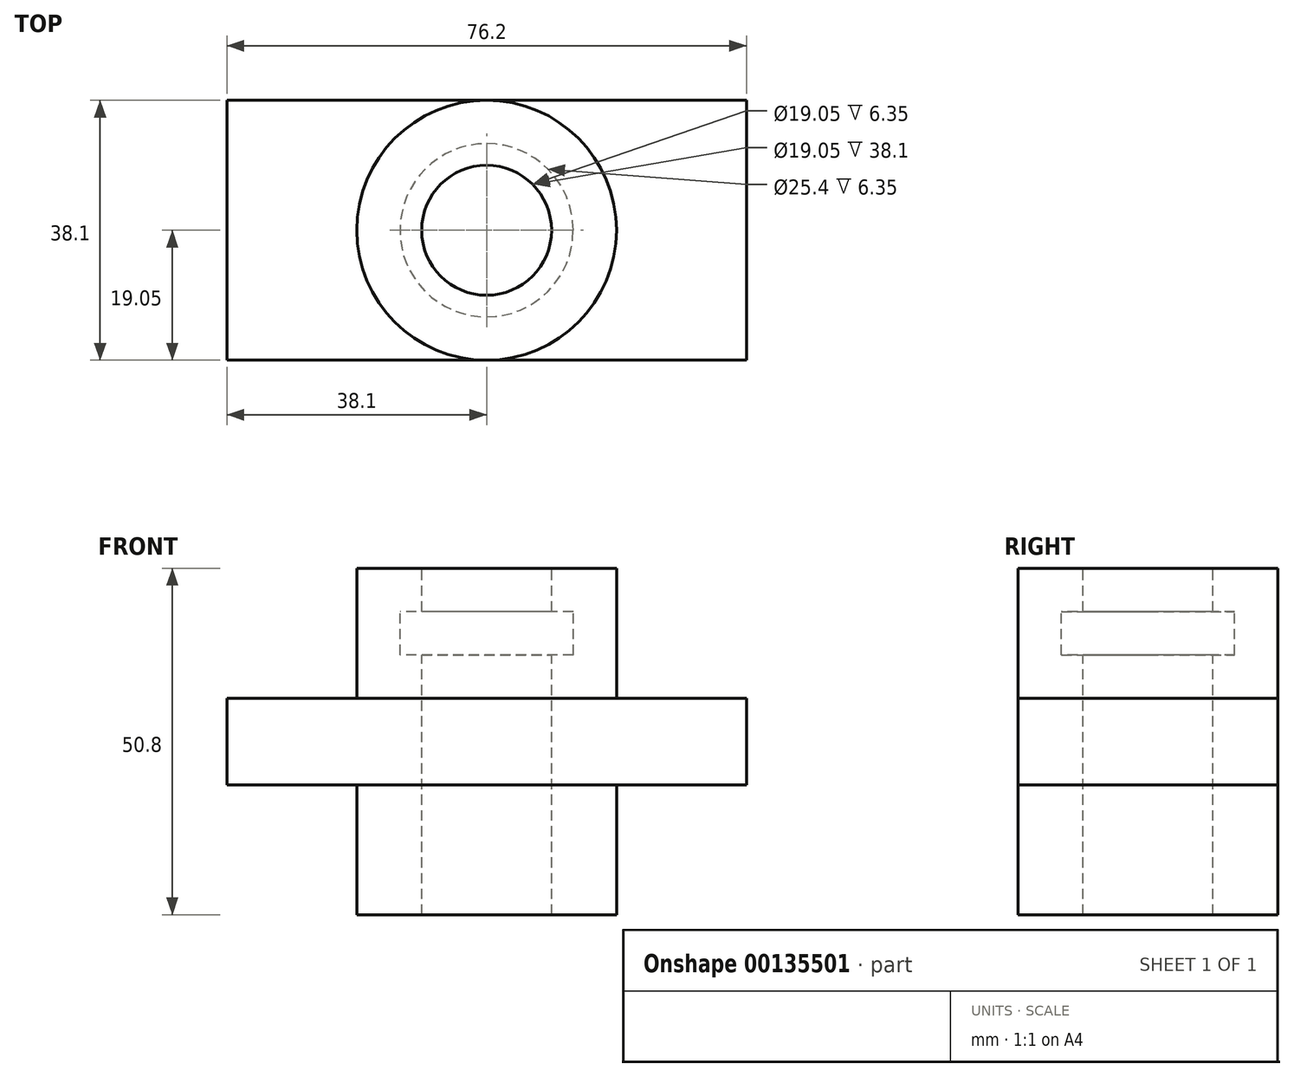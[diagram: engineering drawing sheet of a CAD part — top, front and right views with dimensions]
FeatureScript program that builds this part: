
annotation { "Feature Type Name" : "Feature", "Feature Type Description" : "" }
export const myFeature = defineFeature(function(context is Context, id is Id, definition is map)
    precondition{}
    {
        {
            var Q0;
            Q0=qCreatedBy(makeId("Top.planeOp"),FACE);
            var sketch = newSketch(context, id + "F0", { "sketchPlane" : qUnion([Q0])});
            skLineSegment(sketch, "E0.bottom", {"start": v(38.1, 19.05) * mm, "end": v(-38.1, 19.05) * mm});
            skLineSegment(sketch, "E0.top", {"start": v(38.1, -19.05) * mm, "end": v(-38.1, -19.05) * mm});
            skLineSegment(sketch, "E0.left", {"start": v(38.1, 19.05) * mm, "end": v(38.1, -19.05) * mm});
            skLineSegment(sketch, "E0.right", {"start": v(-38.1, 19.05) * mm, "end": v(-38.1, -19.05) * mm});
            skPoint(sketch, "E0.middle", {"position": v(0, 0) * mm});
            skSolve(sketch);
        }
        {
            var Q0;
            Q0 = qSketchRegion(id + "F0", true);
            extrude(context, id + "F1", {"entities" : qUnion([Q0]), "depth" : 12.7 * mm});
        }
        {
            var Q0;
            Q0=makeQuery(id+"F1.opExtrude","CAP_FACE",FACE,{"disambiguationData":[OSD([sQuery(id+"F0.wireOp",EDGE,"E0.bottom"),sQuery(id+"F0.wireOp",EDGE,"E0.top"),sQuery(id+"F0.wireOp",EDGE,"E0.left"),sQuery(id+"F0.wireOp",EDGE,"E0.right")])],"isStart":true});
            var sketch = newSketch(context, id + "F2", { "sketchPlane" : qUnion([Q0])});
            skCircle(sketch, "E1", {"center": v(0, 0) * mm, "radius": 19.05 * mm});
            skCircle(sketch, "E2", {"center": v(0, 0) * mm, "radius": 9.53 * mm});
            skSolve(sketch);
        }
        {
            var Q0;
            Q0 = qSketchRegion(id + "F2", true);
            extrude(context, id + "F3", {"entities" : qUnion([Q0]), "operationType" : NewBodyOperationType.ADD, "depth" : 19.05 * mm, "hasSecondDirection" : true, "secondDirectionOppositeDirection" : true, "secondDirectionDepth" : 31.75 * mm});
        }
        {
            var Q0;
            Q0=qCreatedBy(makeId("Right.planeOp"),FACE);
            var sketch = newSketch(context, id + "F4", { "sketchPlane" : qUnion([Q0])});
            skLineSegment(sketch, "E3", {"start": v(0, 0) * mm, "end": v(-12.7, 0) * mm, "construction": true});
            skLineSegment(sketch, "E4", {"start": v(-12.7, 0) * mm, "end": v(-12.7, 19.05) * mm, "construction": true});
            skLineSegment(sketch, "E5", {"start": v(-12.7, 19.05) * mm, "end": v(0, 19.05) * mm});
            skLineSegment(sketch, "E6", {"start": v(0, 25.4) * mm, "end": v(-12.7, 25.4) * mm});
            skLineSegment(sketch, "E7", {"start": v(-12.7, 25.4) * mm, "end": v(-12.7, 19.05) * mm});
            skLineSegment(sketch, "E8", {"start": v(0, 0) * mm, "end": v(0, 32.42) * mm, "construction": true});
            skPoint(sketch, "E8.endSnap0", {"position": v(0, 25.4) * mm});
            skLineSegment(sketch, "E9", {"start": v(0, 25.4) * mm, "end": v(0, 19.05) * mm});
            skSolve(sketch);
        }
        {
            var Q0;
            Q0=makeQuery(id+"F4.imprint","IMPRINT",FACE,{"disambiguationData":[TD([[makeQuery(id+"F4.imprint","IMPRINT",EDGE,{"derivedFrom":sQuery(id+"F4.wireOp",EDGE,"E5")}),1.0]])]});
            var Q1;
            Q1=sQuery(id+"F4.wireOp",EDGE,"E8");
            revolve(context, id + "F5", {"operationType" : NewBodyOperationType.REMOVE, "entities" : qUnion([Q0]), "axis" : qUnion([Q1]), "revolveType" : RevolveType.FULL, "oppositeDirection" : true});
        }
        {
            var Q0;
            Q0=makeQuery(id+"F3.boolean.opBoolean","SPLIT",FACE,{"disambiguationData":[TD([makeQuery(id+"F3.opExtrude","SWEPT_FACE",FACE,{"disambiguationData":[OSD([sQuery(id+"F2.wireOp",EDGE,"E2")])]})])],"derivedFrom":makeQuery(id+"F1.opExtrude","CAP_FACE",FACE,{"disambiguationData":[OSD([sQuery(id+"F0.wireOp",EDGE,"E0.bottom"),sQuery(id+"F0.wireOp",EDGE,"E0.top"),sQuery(id+"F0.wireOp",EDGE,"E0.left"),sQuery(id+"F0.wireOp",EDGE,"E0.right")])],"isStart":true})});
            extrude(context, id + "F6", {"entities" : qUnion([Q0]), "operationType" : NewBodyOperationType.REMOVE, "endBound" : BoundingType.THROUGH_ALL, "oppositeDirection" : true, "depth" : 25.4 * mm});
        }
    });
